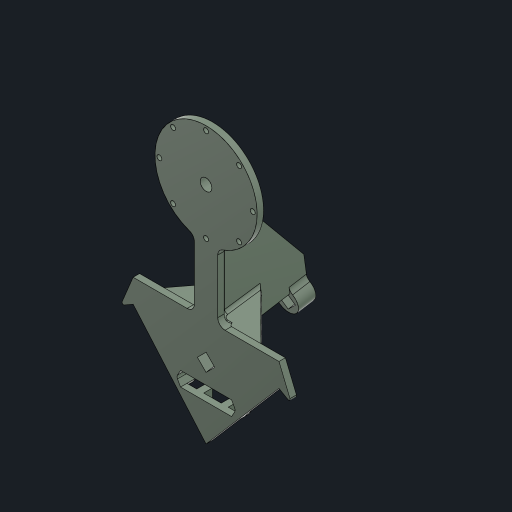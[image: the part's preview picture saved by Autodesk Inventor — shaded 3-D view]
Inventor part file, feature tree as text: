
AUTODESK INVENTOR PART (.ipt)
format: ipt  version: 2023 (Build 270158000, 158)  size: 538,624 bytes
history: native  units: mm
features: extrude x17, sketch x16, other x6, fillet x3, projected_geometry x2, mirror x1, hole x1, pattern_circular x1
ambient origin geometry x8: Origin, YZ Plane, XZ Plane, XY Plane, X Axis, Y Axis, Z Axis, Center Point
bodies: Body1 (feature_tree)
feature tree (47):
  other  "ソリッド1"
  sketch  "スケッチ1"
  extrude  "押し出し1"  Depth=2.2mm
  extrude  "押し出し2"  Depth=40.0mm
  extrude  "押し出し4"  Depth=14.3117mm
  extrude  "押し出し5"  Depth=8.0mm
  extrude  "爪"  Depth=180.0mm
  extrude  "押し出し17"  Depth=15.0mm
  extrude  "押し出し20"  Depth=14.0499mm
  extrude  "押し出し21"  Depth=30.0mm
  mirror  "ミラー1"
  extrude  "押し出し6"  Depth=25.0mm TaperAngle=0.0deg
  other  "作業平面2"
  extrude  "押し出し10"  Depth=4.0mm TaperAngle=0.0deg
  extrude  "ロッド穴"  Depth=1.6mm TaperAngle=0.0deg
  other  "作業平面3"
  extrude  "押し出し11"  TaperAngle=0.0deg  [1 undecoded]
  hole  "穴1"  [1 undecoded]
  pattern_circular  "円形状パターン1"  [2 undecoded]
  extrude  "穴延長"  Depth=1.4mm TaperAngle=0.0deg
  extrude  "押し出し12"  Depth=1.0mm
  extrude  "押し出し13"  Depth=4.2mm
  fillet  "フィレット2"  [1 undecoded]
  other  "YZ平面"
  other  "XZ平面"
  extrude  "押し出し22"  Depth=8.0mm
  fillet  "フィレット3"  Radius=5.0mm
  fillet  "フィレット4"  Radius=6.0mm
  extrude  "押し出し23"  Depth=32.0mm
  sketch  "スケッチ2"
  sketch  "スケッチ3"
  other  "作業平面1"
  sketch  "スケッチ6"
  sketch  "スケッチ7"
  sketch  "スケッチ8"
  projected_geometry  "投影ループ1"
  sketch  "スケッチ9"
  sketch  "スケッチ10"
  sketch  "スケッチ11"
  sketch  "スケッチ15"
  sketch  "スケッチ16"
  sketch  "スケッチ19"
  sketch  "スケッチ21"
  sketch  "スケッチ22"
  projected_geometry  "投影ループ2"
  sketch  "スケッチ23"
  sketch  "スケッチ24"
note: 5 required parameter values undecoded (feature->parameter linkage not recoverable at this tier; creation-order binding heuristic only, values carry confidence <= 0.55)
